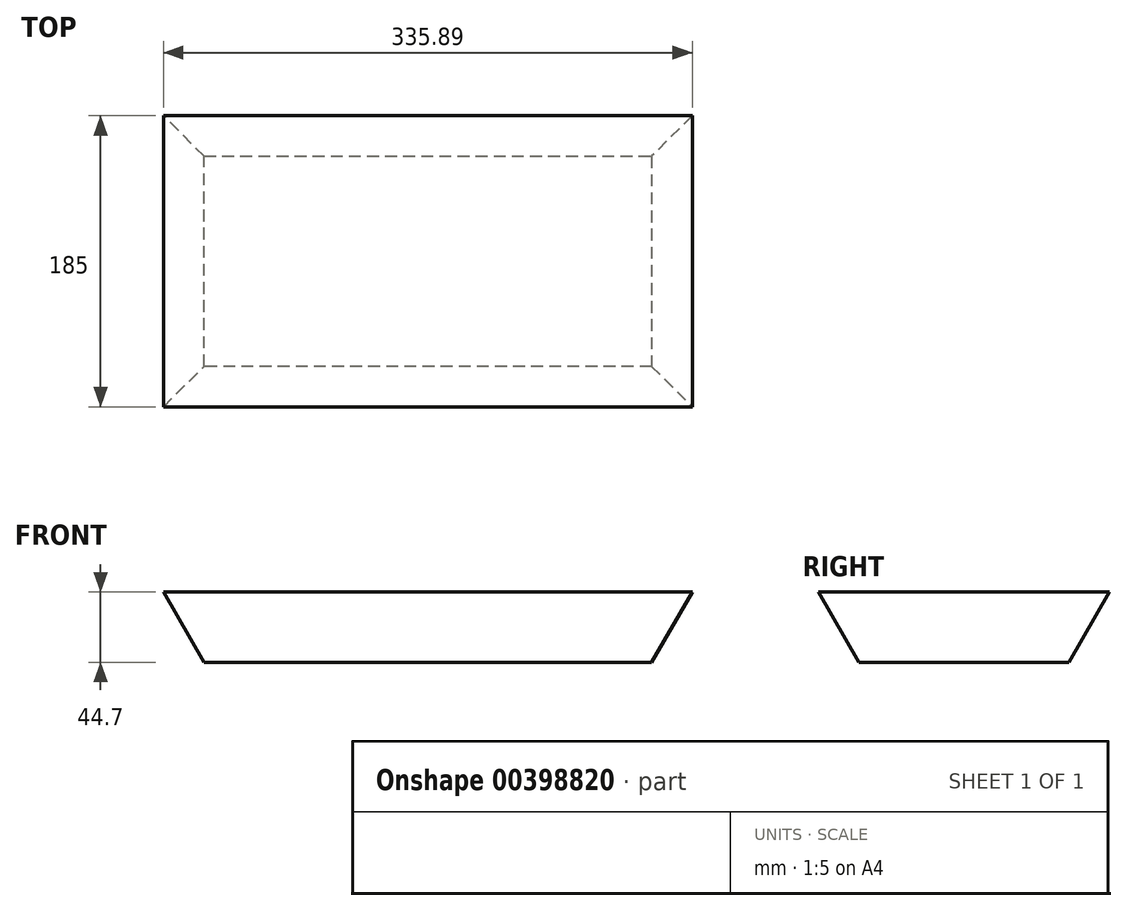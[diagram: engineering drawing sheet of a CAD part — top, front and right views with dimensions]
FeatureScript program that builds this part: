
annotation { "Feature Type Name" : "Feature", "Feature Type Description" : "" }
export const myFeature = defineFeature(function(context is Context, id is Id, definition is map)
    precondition{}
    {
        {
            var Q0;
            Q0=qCreatedBy(makeId("Top.planeOp"),FACE);
            var sketch = newSketch(context, id + "F0", { "sketchPlane" : qUnion([Q0])});
            skLineSegment(sketch, "E0.bottom", {"start": v(-137.25, 58.23) * mm, "end": v(147.02, 58.23) * mm});
            skLineSegment(sketch, "E0.top", {"start": v(-137.25, -75.15) * mm, "end": v(147.02, -75.15) * mm});
            skLineSegment(sketch, "E0.left", {"start": v(-137.25, 58.23) * mm, "end": v(-137.25, -75.15) * mm});
            skLineSegment(sketch, "E0.right", {"start": v(147.02, 58.23) * mm, "end": v(147.02, -75.15) * mm});
            skSolve(sketch);
        }
        {
            var Q0;
            Q0 = qSketchRegion(id + "F0", true);
            extrude(context, id + "F1", {"entities" : qUnion([Q0]), "depth" : 44.7 * mm, "hasDraft" : true, "draftAngle" : 30 * degree});
        }
    });
